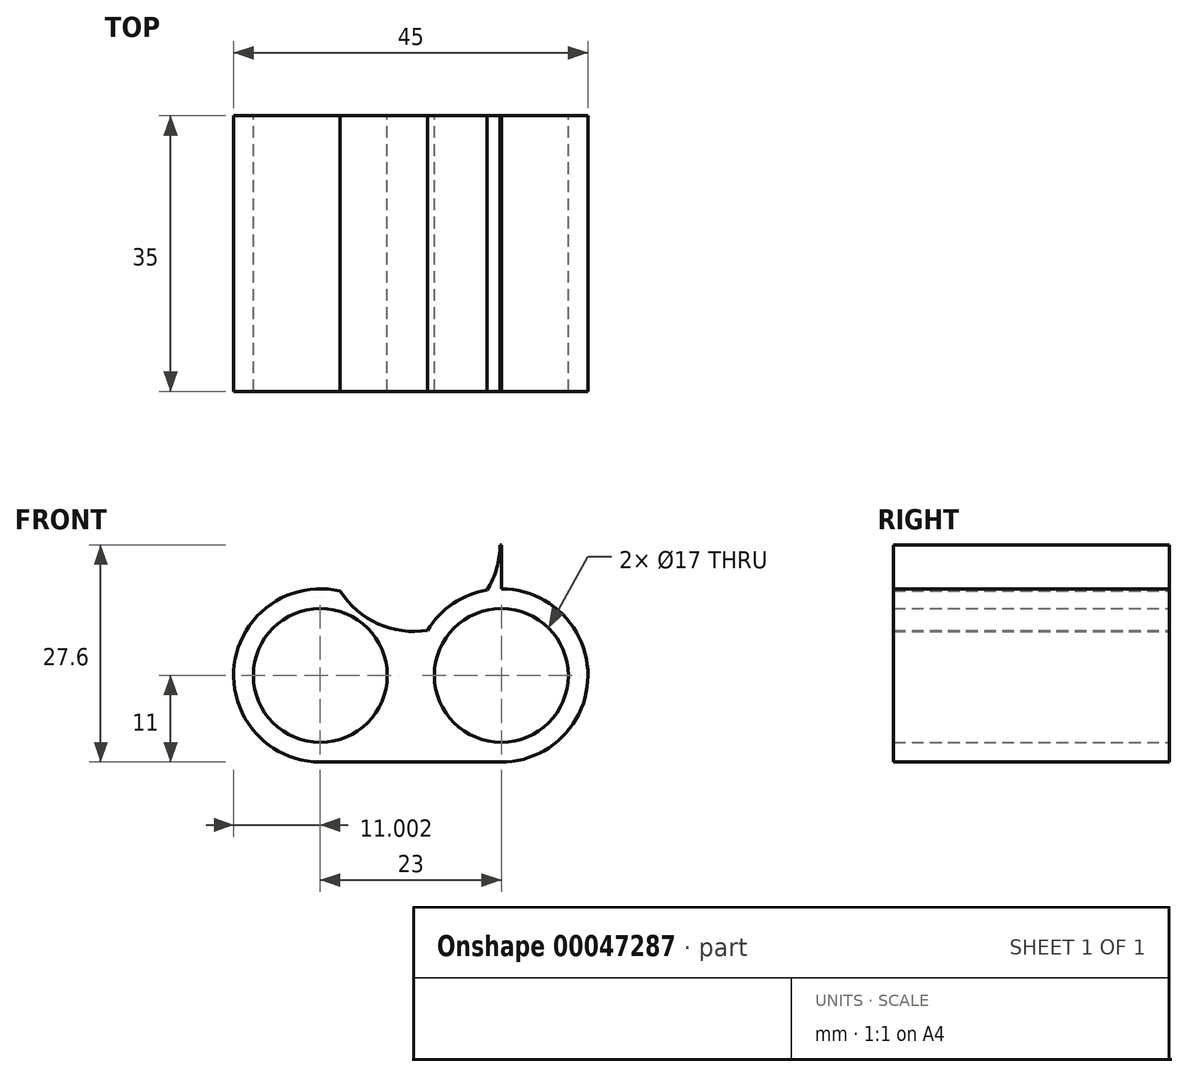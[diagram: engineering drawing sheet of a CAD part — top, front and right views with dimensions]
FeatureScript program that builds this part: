
annotation { "Feature Type Name" : "Feature", "Feature Type Description" : "" }
export const myFeature = defineFeature(function(context is Context, id is Id, definition is map)
    precondition{}
    {
        {
            var Q0;
            Q0=qCreatedBy(makeId("Front.planeOp"),FACE);
            var sketch = newSketch(context, id + "F0", { "sketchPlane" : qUnion([Q0])});
            skLineSegment(sketch, "E0.bottom", {"start": v(-11.83, 16.6) * mm, "end": v(11.17, 16.6) * mm});
            skLineSegment(sketch, "E0.top", {"start": v(-11.83, -8.4) * mm, "end": v(11.17, -8.4) * mm});
            skLineSegment(sketch, "E0.left", {"start": v(-11.83, 16.6) * mm, "end": v(-11.83, -8.4) * mm});
            skLineSegment(sketch, "E0.right", {"start": v(11.17, 16.6) * mm, "end": v(11.17, -8.4) * mm});
            skCircle(sketch, "E1", {"center": v(0, 16.6) * mm, "radius": 8.5 * mm});
            skCircle(sketch, "E2", {"center": v(11.17, 0) * mm, "radius": 8.5 * mm});
            skCircle(sketch, "E3", {"center": v(-11.83, 0) * mm, "radius": 8.5 * mm});
            skPoint(sketch, "E3.centerSnap0", {"position": v(-11.83, 4.1) * mm});
            skCircle(sketch, "E4", {"center": v(-11.83, 0) * mm, "radius": 11 * mm});
            skCircle(sketch, "E5", {"center": v(11.17, 0) * mm, "radius": 11 * mm});
            skCircle(sketch, "E6", {"center": v(0, 16.6) * mm, "radius": 11 * mm});
            skLineSegment(sketch, "E7", {"start": v(-11.92, -11) * mm, "end": v(11.26, -11) * mm});
            skSolve(sketch);
        }
        {
            var Q0;
            {var subQ0=sQuery(id+"F0.wireOp",EDGE,"E7");var subQ1=sQuery(id+"F0.wireOp",EDGE,"E4");var subQ3=makeQuery(id+"F0.imprint","INTERSECT",VERTEX,{"disambiguationData":[OD(0.0)],"derivedFrom":[subQ1,subQ0]});Q0=makeQuery(id+"F0.imprint","IMPRINT",FACE,{"disambiguationData":[TD([[makeQuery(id+"F0.imprint","IMPRINT",EDGE,{"disambiguationData":[TD([[subQ3,-1.0]])],"derivedFrom":subQ1}),1.0]])]});}
            var Q1;
            {var subQ0=sQuery(id+"F0.wireOp",EDGE,"E7");var subQ1=sQuery(id+"F0.wireOp",EDGE,"E5");var subQ3=makeQuery(id+"F0.imprint","INTERSECT",VERTEX,{"disambiguationData":[OD(0.0)],"derivedFrom":[subQ1,subQ0]});Q1=makeQuery(id+"F0.imprint","IMPRINT",FACE,{"disambiguationData":[TD([[makeQuery(id+"F0.imprint","IMPRINT",EDGE,{"disambiguationData":[TD([[subQ3,1.0]])],"derivedFrom":subQ1}),1.0]])]});}
            var Q2;
            {var subQ0=sQuery(id+"F0.wireOp",EDGE,"E6");var subQ1=sQuery(id+"F0.wireOp",EDGE,"E0.bottom");var subQ3=makeQuery(id+"F0.imprint","INTERSECT",VERTEX,{"disambiguationData":[OD(0.0)],"derivedFrom":[subQ1,subQ0]});Q2=makeQuery(id+"F0.imprint","IMPRINT",FACE,{"disambiguationData":[TD([[makeQuery(id+"F0.imprint","IMPRINT",EDGE,{"disambiguationData":[TD([[subQ3,-1.0]])],"derivedFrom":subQ1}),1.0]])]});}
            var Q3;
            {var subQ3=sQuery(id+"F0.wireOp",EDGE,"E4");var subQ5=sQuery(id+"F0.wireOp",EDGE,"E0.top");var subQ6=makeQuery(id+"F0.imprint","INTERSECT",VERTEX,{"derivedFrom":[subQ5,subQ3]});Q3=makeQuery(id+"F0.imprint","IMPRINT",FACE,{"disambiguationData":[TD([[makeQuery(id+"F0.imprint","IMPRINT",EDGE,{"disambiguationData":[TD([[subQ6,-1.0]])],"derivedFrom":subQ5}),-1.0]])]});}
            var Q4;
            {var subQ0=sQuery(id+"F0.wireOp",EDGE,"E6");var subQ3=sQuery(id+"F0.wireOp",EDGE,"E0.bottom");var subQ9=makeQuery(id+"F0.imprint","INTERSECT",VERTEX,{"disambiguationData":[OD(0.0)],"derivedFrom":[subQ3,subQ0]});Q4=makeQuery(id+"F0.imprint","IMPRINT",FACE,{"disambiguationData":[TD([[makeQuery(id+"F0.imprint","IMPRINT",EDGE,{"disambiguationData":[TD([[subQ9,-1.0]])],"derivedFrom":subQ3}),-1.0]])]});}
            var Q5;
            {var subQ0=sQuery(id+"F0.wireOp",EDGE,"E6");var subQ1=sQuery(id+"F0.wireOp",EDGE,"E4");var subQ3=makeQuery(id+"F0.imprint","INTERSECT",VERTEX,{"disambiguationData":[OD(0.0)],"derivedFrom":[subQ1,subQ0]});Q5=makeQuery(id+"F0.imprint","IMPRINT",FACE,{"disambiguationData":[TD([[makeQuery(id+"F0.imprint","IMPRINT",EDGE,{"disambiguationData":[TD([[subQ3,1.0]])],"derivedFrom":subQ1}),1.0]])]});}
            var Q6;
            {var subQ0=sQuery(id+"F0.wireOp",EDGE,"E6");var subQ1=sQuery(id+"F0.wireOp",EDGE,"E5");var subQ3=makeQuery(id+"F0.imprint","INTERSECT",VERTEX,{"disambiguationData":[OD(0.0)],"derivedFrom":[subQ1,subQ0]});Q6=makeQuery(id+"F0.imprint","IMPRINT",FACE,{"disambiguationData":[TD([[makeQuery(id+"F0.imprint","IMPRINT",EDGE,{"disambiguationData":[TD([[subQ3,-1.0]])],"derivedFrom":subQ1}),1.0]])]});}
            var Q7;
            {var subQ3=sQuery(id+"F0.wireOp",EDGE,"E4");var subQ5=sQuery(id+"F0.wireOp",EDGE,"E0.top");var subQ7=makeQuery(id+"F0.imprint","INTERSECT",VERTEX,{"derivedFrom":[subQ5,subQ3]});Q7=makeQuery(id+"F0.imprint","IMPRINT",FACE,{"disambiguationData":[TD([[makeQuery(id+"F0.imprint","IMPRINT",EDGE,{"disambiguationData":[TD([[subQ7,-1.0]])],"derivedFrom":subQ5}),1.0]])]});}
            var Q8;
            {var subQ1=sQuery(id+"F0.wireOp",EDGE,"E5");var subQ4=sQuery(id+"F0.wireOp",EDGE,"E0.top");var subQ5=makeQuery(id+"F0.imprint","INTERSECT",VERTEX,{"derivedFrom":[subQ4,subQ1]});Q8=makeQuery(id+"F0.imprint","IMPRINT",FACE,{"disambiguationData":[TD([[makeQuery(id+"F0.imprint","IMPRINT",EDGE,{"disambiguationData":[TD([[subQ5,-1.0]])],"derivedFrom":subQ4}),1.0]])]});}
            var Q9;
            {var subQ4=sQuery(id+"F0.wireOp",EDGE,"E0.top");var subQ6=sQuery(id+"F0.wireOp",EDGE,"E3");var subQ7=makeQuery(id+"F0.imprint","INTERSECT",VERTEX,{"derivedFrom":[subQ4,subQ6]});Q9=makeQuery(id+"F0.imprint","IMPRINT",FACE,{"disambiguationData":[TD([[makeQuery(id+"F0.imprint","IMPRINT",EDGE,{"disambiguationData":[TD([[subQ7,-1.0]])],"derivedFrom":subQ4}),1.0]])]});}
            var Q10;
            {var subQ0=sQuery(id+"F0.wireOp",EDGE,"E5");var subQ5=sQuery(id+"F0.wireOp",EDGE,"E0.top");var subQ8=makeQuery(id+"F0.imprint","INTERSECT",VERTEX,{"derivedFrom":[subQ5,subQ0]});Q10=makeQuery(id+"F0.imprint","IMPRINT",FACE,{"disambiguationData":[TD([[makeQuery(id+"F0.imprint","IMPRINT",EDGE,{"disambiguationData":[TD([[subQ8,-1.0]])],"derivedFrom":subQ5}),-1.0]])]});}
            var Q11;
            {var subQ4=sQuery(id+"F0.wireOp",EDGE,"E0.top");var subQ6=sQuery(id+"F0.wireOp",EDGE,"E3");var subQ7=makeQuery(id+"F0.imprint","INTERSECT",VERTEX,{"derivedFrom":[subQ4,subQ6]});Q11=makeQuery(id+"F0.imprint","IMPRINT",FACE,{"disambiguationData":[TD([[makeQuery(id+"F0.imprint","IMPRINT",EDGE,{"disambiguationData":[TD([[subQ7,-1.0]])],"derivedFrom":subQ4}),-1.0]])]});}
            extrude(context, id + "F1", {"entities" : qUnion([Q0, Q1, Q2, Q3, Q4, Q5, Q6, Q7, Q8, Q9, Q10, Q11]), "depth" : 35 * mm});
        }
    });
